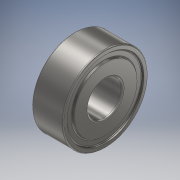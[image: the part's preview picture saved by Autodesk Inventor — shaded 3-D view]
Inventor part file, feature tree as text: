
AUTODESK INVENTOR PART (.ipt)
format: ipt  version: 2019 (Build 230136000, 136)  size: 233,984 bytes
history: native  units: mm
features: revolve x1, sketch x1
ambient origin geometry x8: Origin, YZ Plane, XZ Plane, XY Plane, X Axis, Y Axis, Z Axis, Center Point
bodies: Body1 (feature_tree)
feature tree (2):
  revolve  "Revolution1"  [1 undecoded]
  sketch  "Sketch1"  dims[d2=55.0mm d3=22.0mm d4=40.7mm d5=49.647869mm d6=49.59288mm d7=90.0deg]
note: 1 required parameter value undecoded (feature->parameter linkage not recoverable at this tier; creation-order binding heuristic only, values carry confidence <= 0.55)
